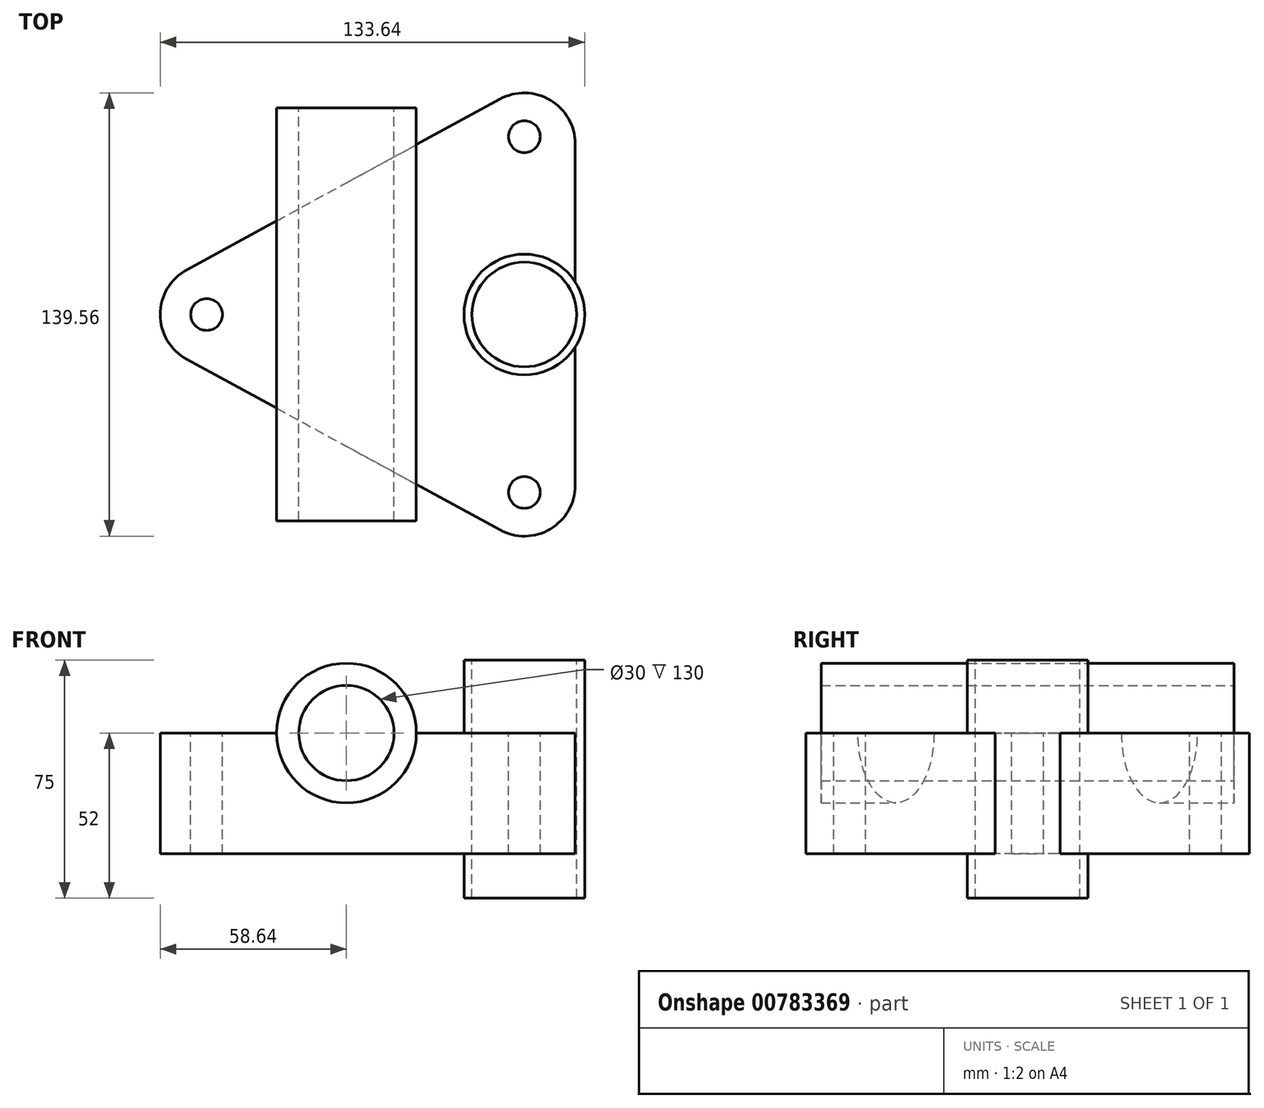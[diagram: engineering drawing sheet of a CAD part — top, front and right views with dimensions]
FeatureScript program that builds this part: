
annotation { "Feature Type Name" : "Feature", "Feature Type Description" : "" }
export const myFeature = defineFeature(function(context is Context, id is Id, definition is map)
    precondition{}
    {
        {
            var Q0;
            Q0=qCreatedBy(makeId("Front.planeOp"),FACE);
            var sketch = newSketch(context, id + "F0", { "sketchPlane" : qUnion([Q0])});
            skCircle(sketch, "E0", {"center": v(0, 0) * mm, "radius": 15 * mm});
            skCircle(sketch, "E1", {"center": v(0, 0) * mm, "radius": 22 * mm});
            skLineSegment(sketch, "E2", {"start": v(-22, 0) * mm, "end": v(-57.06, 0) * mm});
            skLineSegment(sketch, "E3", {"start": v(-57.06, 0) * mm, "end": v(-57.06, -38) * mm});
            skLineSegment(sketch, "E4", {"start": v(75, -52) * mm, "end": v(75, 23) * mm});
            skLineSegment(sketch, "E5", {"start": v(75, 23) * mm, "end": v(37, 23) * mm});
            skLineSegment(sketch, "E6", {"start": v(37, 23) * mm, "end": v(37, 0) * mm});
            skLineSegment(sketch, "E7", {"start": v(37, 0) * mm, "end": v(22, 0) * mm});
            skLineSegment(sketch, "E8", {"start": v(75, -52) * mm, "end": v(37, -52) * mm});
            skLineSegment(sketch, "E9", {"start": v(37, -52) * mm, "end": v(37, -38) * mm});
            skLineSegment(sketch, "E10", {"start": v(37, -38) * mm, "end": v(-57.06, -38) * mm});
            skLineSegment(sketch, "E11", {"start": v(13.96, -17) * mm, "end": v(72, -17) * mm});
            skLineSegment(sketch, "E12", {"start": v(37, -38) * mm, "end": v(72, -38) * mm});
            skLineSegment(sketch, "E13", {"start": v(72, -17) * mm, "end": v(72, -38) * mm});
            skLineSegment(sketch, "E14", {"start": v(56, 23) * mm, "end": v(56, -52) * mm, "construction": true});
            skLineSegment(sketch, "E15", {"start": v(43.5, 23) * mm, "end": v(43.5, -17) * mm});
            skLineSegment(sketch, "E16", {"start": v(43.5, -38) * mm, "end": v(43.5, -52) * mm});
            skLineSegment(sketch, "E17.MirrorCS", {"start": v(68.5, 23) * mm, "end": v(68.5, -17) * mm});
            skLineSegment(sketch, "E18.MirrorCS", {"start": v(68.5, -38) * mm, "end": v(68.5, -52) * mm});
            skLineSegment(sketch, "E19", {"start": v(39.5, 23) * mm, "end": v(39.5, -17) * mm});
            skLineSegment(sketch, "E20", {"start": v(39.5, -38) * mm, "end": v(39.5, -52) * mm});
            skLineSegment(sketch, "E21.MirrorCS", {"start": v(72.5, 23) * mm, "end": v(72.5, -17) * mm});
            skLineSegment(sketch, "E22.MirrorCS", {"start": v(72.5, -38) * mm, "end": v(72.5, -52) * mm});
            skLineSegment(sketch, "E23", {"start": v(72.5, -17) * mm, "end": v(72.5, -38) * mm});
            skLineSegment(sketch, "E24", {"start": v(37, 0) * mm, "end": v(37, -17) * mm});
            skSolve(sketch);
        }
        {
            var Q0;
            Q0=qCreatedBy(makeId("Top.planeOp"),FACE);
            var sketch = newSketch(context, id + "F1", { "sketchPlane" : qUnion([Q0])});
            skCircle(sketch, "E25", {"center": v(56, 56) * mm, "radius": 5 * mm});
            skCircle(sketch, "E26.MirrorC", {"center": v(56, -56) * mm, "radius": 5 * mm});
            skCircle(sketch, "E27", {"center": v(56, 0) * mm, "radius": 19 * mm, "construction": true});
            skCircle(sketch, "E28", {"center": v(56, 0) * mm, "radius": 16.5 * mm});
            skCircle(sketch, "E29", {"center": v(-44, 0) * mm, "radius": 5 * mm});
            skLineSegment(sketch, "E30", {"start": v(0, 65) * mm, "end": v(22, 65) * mm, "construction": true});
            skLineSegment(sketch, "E31", {"start": v(22, 65) * mm, "end": v(22, -65) * mm, "construction": true});
            skLineSegment(sketch, "E32", {"start": v(22, -65) * mm, "end": v(0, -65) * mm, "construction": true});
            skLineSegment(sketch, "E33.MirrorCS", {"start": v(0, 65) * mm, "end": v(-22, 65) * mm, "construction": true});
            skLineSegment(sketch, "E34.MirrorCS", {"start": v(-22, 65) * mm, "end": v(-22, -65) * mm, "construction": true});
            skLineSegment(sketch, "E35.MirrorCS", {"start": v(-22, -65) * mm, "end": v(0, -65) * mm, "construction": true});
            skLineSegment(sketch, "E36", {"start": v(72, 0) * mm, "end": v(72, 80.72) * mm});
            skLineSegment(sketch, "E37.MirrorCS", {"start": v(72, 0) * mm, "end": v(72, -80.72) * mm});
            skLineSegment(sketch, "E38", {"start": v(-76.07, 0) * mm, "end": v(72, 80.72) * mm});
            skLineSegment(sketch, "E39", {"start": v(-76.07, 0) * mm, "end": v(72, -80.72) * mm});
            skPoint(sketch, "E40", {"position": v(56, 72) * mm});
            skLineSegment(sketch, "E41", {"start": v(-22, 29.48) * mm, "end": v(-22, -29.48) * mm});
            skLineSegment(sketch, "E42", {"start": v(22, 53.46) * mm, "end": v(22, -53.46) * mm});
            skPoint(sketch, "E43", {"position": v(56, -72) * mm});
            skLineSegment(sketch, "E44", {"start": v(-44, 0) * mm, "end": v(-55.31, 11.31) * mm, "construction": true});
            skLineSegment(sketch, "E45", {"start": v(-44, 0) * mm, "end": v(-55.31, -11.31) * mm, "construction": true});
            skSolve(sketch);
        }
        {
            var Q0;
            {var subQ1=sQuery(id+"F0.wireOp",EDGE,"E4");Q0=makeQuery(id+"F0.imprint","IMPRINT",FACE,{"disambiguationData":[TD([[makeQuery(id+"F0.imprint","IMPRINT",EDGE,{"derivedFrom":subQ1}),1.0]])]});}
            var Q1;
            Q1=sQuery(id+"F0.wireOp",EDGE,"E14");
            revolve(context, id + "F2", {"surfaceOperationType" : NewSurfaceOperationType.NEW, "entities" : qUnion([Q0]), "axis" : qUnion([Q1]), "revolveType" : RevolveType.FULL});
        }
        {
            var Q0;
            Q0=makeQuery(id+"F1.imprint","IMPRINT",FACE,{"disambiguationData":[TD([[makeQuery(id+"F1.imprint","IMPRINT",EDGE,{"derivedFrom":sQuery(id+"F1.wireOp",EDGE,"E29")}),-1.0]])]});
            var Q1;
            {var subQ0=sQuery(id+"F1.wireOp",EDGE,"E41");Q1=makeQuery(id+"F1.imprint","IMPRINT",FACE,{"disambiguationData":[TD([[makeQuery(id+"F1.imprint","IMPRINT",EDGE,{"derivedFrom":subQ0}),1.0]])]});}
            var Q2;
            Q2=makeQuery(id+"F1.imprint","IMPRINT",FACE,{"disambiguationData":[TD([[makeQuery(id+"F1.imprint","IMPRINT",EDGE,{"derivedFrom":sQuery(id+"F1.wireOp",EDGE,"E25")}),-1.0]])]});
            extrude(context, id + "F3", {"entities" : qUnion([Q0, Q1, Q2]), "operationType" : NewBodyOperationType.ADD, "oppositeDirection" : true, "depth" : 38 * mm, "offsetDistance" : 25 * mm});
        }
        {
            var Q0;
            Q0=makeQuery(id+"F0.imprint","IMPRINT",FACE,{"disambiguationData":[TD([[makeQuery(id+"F0.imprint","IMPRINT",EDGE,{"derivedFrom":sQuery(id+"F0.wireOp",EDGE,"E0")}),1.0]])]});
            extrude(context, id + "F4", {"entities" : qUnion([Q0]), "operationType" : NewBodyOperationType.REMOVE, "endBound" : BoundingType.SYMMETRIC, "depth" : 130 * mm, "offsetDistance" : 25 * mm});
        }
        {
            var Q0;
            Q0=makeQuery(id+"F0.imprint","IMPRINT",FACE,{"disambiguationData":[TD([[makeQuery(id+"F0.imprint","IMPRINT",EDGE,{"derivedFrom":sQuery(id+"F0.wireOp",EDGE,"E0")}),-1.0]])]});
            extrude(context, id + "F5", {"entities" : qUnion([Q0]), "operationType" : NewBodyOperationType.ADD, "endBound" : BoundingType.SYMMETRIC, "depth" : 130 * mm, "offsetDistance" : 25 * mm});
        }
        {
            var Q0;
            {var subQ0=sQuery(id+"F1.wireOp",EDGE,"E36");var subQ1=sQuery(id+"F1.wireOp",EDGE,"E28");var subQ2=makeQuery(id+"F1.imprint","INTERSECT",VERTEX,{"derivedFrom":[subQ1,subQ0]});Q0=makeQuery(id+"F1.imprint","IMPRINT",FACE,{"disambiguationData":[TD([[makeQuery(id+"F1.imprint","IMPRINT",EDGE,{"disambiguationData":[TD([[subQ2,-1.0]])],"derivedFrom":subQ1}),1.0]])]});}
            extrude(context, id + "F6", {"entities" : qUnion([Q0]), "operationType" : NewBodyOperationType.REMOVE, "endBound" : BoundingType.SYMMETRIC, "depth" : 130 * mm, "offsetDistance" : 25 * mm});
        }
        {
            var Q0;
            Q0=makeQuery(id+"F3.opExtrude","SWEPT_EDGE",EDGE,{"disambiguationData":[OSD([sQuery(id+"F1.wireOp",EDGE,"E38"),sQuery(id+"F1.wireOp",EDGE,"E39")])]});
            var Q1;
            Q1=makeQuery(id+"F3.opExtrude","SWEPT_EDGE",EDGE,{"disambiguationData":[OSD([sQuery(id+"F1.wireOp",EDGE,"E37.MirrorCS"),sQuery(id+"F1.wireOp",EDGE,"E39")])]});
            var Q2;
            Q2=makeQuery(id+"F3.opExtrude","SWEPT_EDGE",EDGE,{"disambiguationData":[OSD([sQuery(id+"F1.wireOp",EDGE,"E36"),sQuery(id+"F1.wireOp",EDGE,"E38")])]});
            fillet(context, id + "F7", {"entities" : qUnion([Q0, Q1, Q2]), "radius" : 16 * mm, "tangentPropagation" : true, "allowEdgeOverflow" : false});
        }
    });
